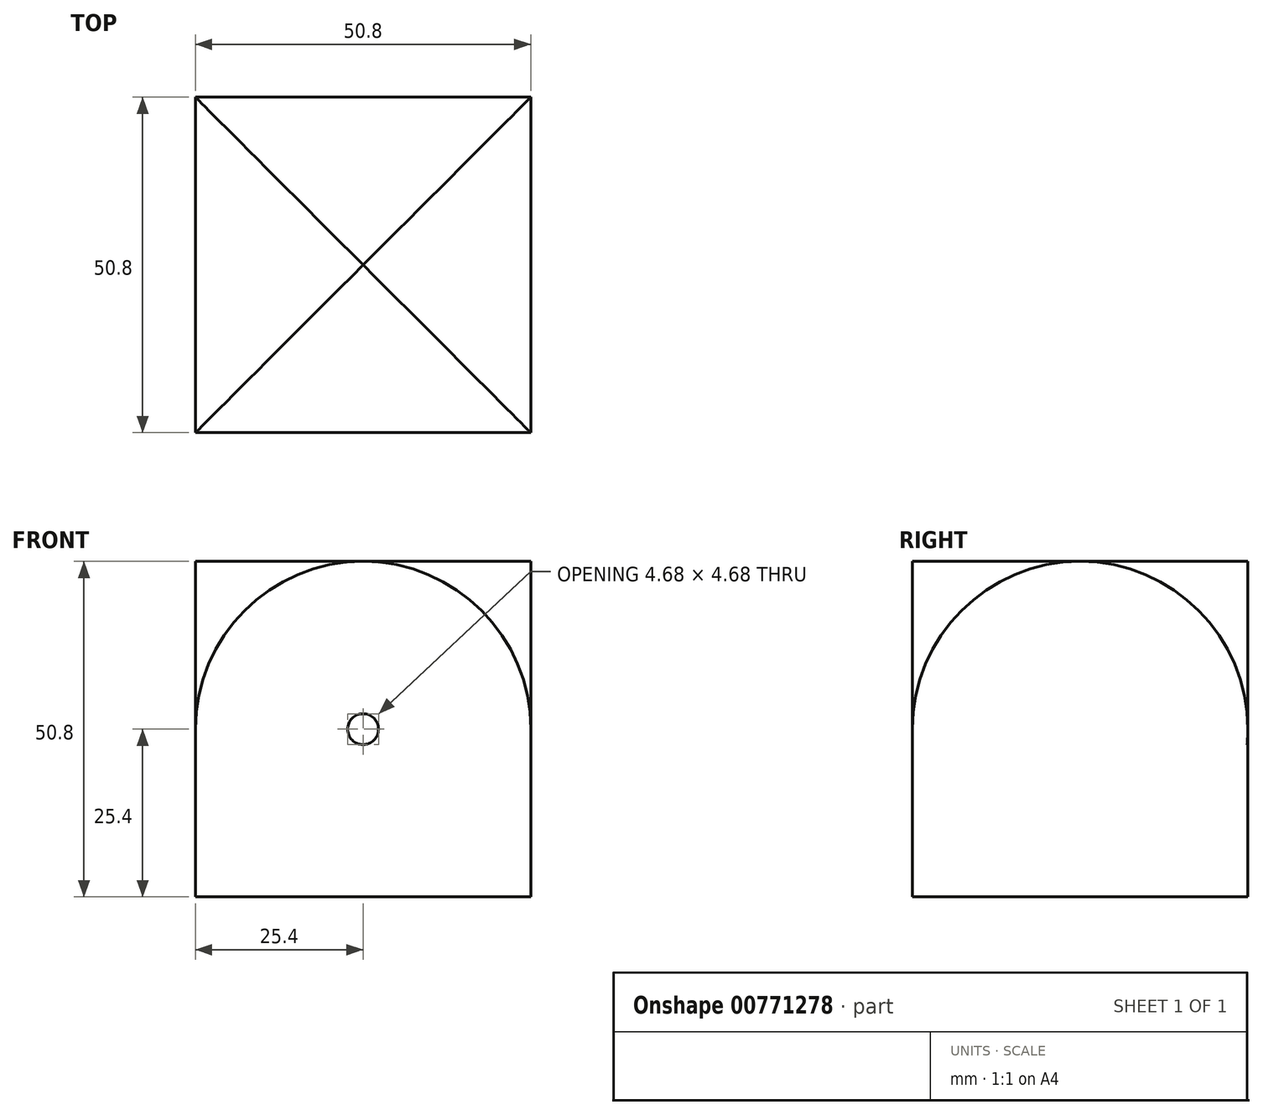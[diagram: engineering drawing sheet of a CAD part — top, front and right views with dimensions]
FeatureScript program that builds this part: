
annotation { "Feature Type Name" : "Feature", "Feature Type Description" : "" }
export const myFeature = defineFeature(function(context is Context, id is Id, definition is map)
    precondition{}
    {
        {
            var Q0;
            Q0=qCreatedBy(makeId("Front.planeOp"),FACE);
            var sketch = newSketch(context, id + "F0", { "sketchPlane" : qUnion([Q0])});
            skLineSegment(sketch, "E0", {"start": v(25.4, 0) * mm, "end": v(25.4, -25.4) * mm});
            skLineSegment(sketch, "E1", {"start": v(25.4, -25.4) * mm, "end": v(-25.4, -25.4) * mm});
            skLineSegment(sketch, "E2", {"start": v(-25.4, -25.4) * mm, "end": v(-25.4, 0) * mm});
            skArc(sketch, "E3", {"start": v(25.4, 0) * mm, "mid": v(0, 25.4) * mm, "end": v(-25.4, 0) * mm});
            skCircle(sketch, "E4", {"center": v(0, 0) * mm, "radius": 2.34 * mm});
            skSolve(sketch);
        }
        {
            var Q0;
            Q0 = qSketchRegion(id + "F0", true);
            extrude(context, id + "F1", {"entities" : qUnion([Q0]), "depth" : 50.8 * mm, "offsetDistance" : 25.4 * mm});
        }
        {
            var Q0;
            Q0=makeQuery(id+"F1.opExtrude","SWEPT_FACE",FACE,{"disambiguationData":[OSD([sQuery(id+"F0.wireOp",EDGE,"E0")])]});
            var sketch = newSketch(context, id + "F2", { "sketchPlane" : qUnion([Q0])});
            skCircle(sketch, "E5", {"center": v(-25.4, 0) * mm, "radius": 25.4 * mm});
            skSolve(sketch);
        }
        {
            var Q0;
            Q0 = qSketchRegion(id + "F2", true);
            extrude(context, id + "F3", {"entities" : qUnion([Q0]), "operationType" : NewBodyOperationType.ADD, "oppositeDirection" : true, "depth" : 50.8 * mm, "offsetDistance" : 25.4 * mm});
        }
    });
